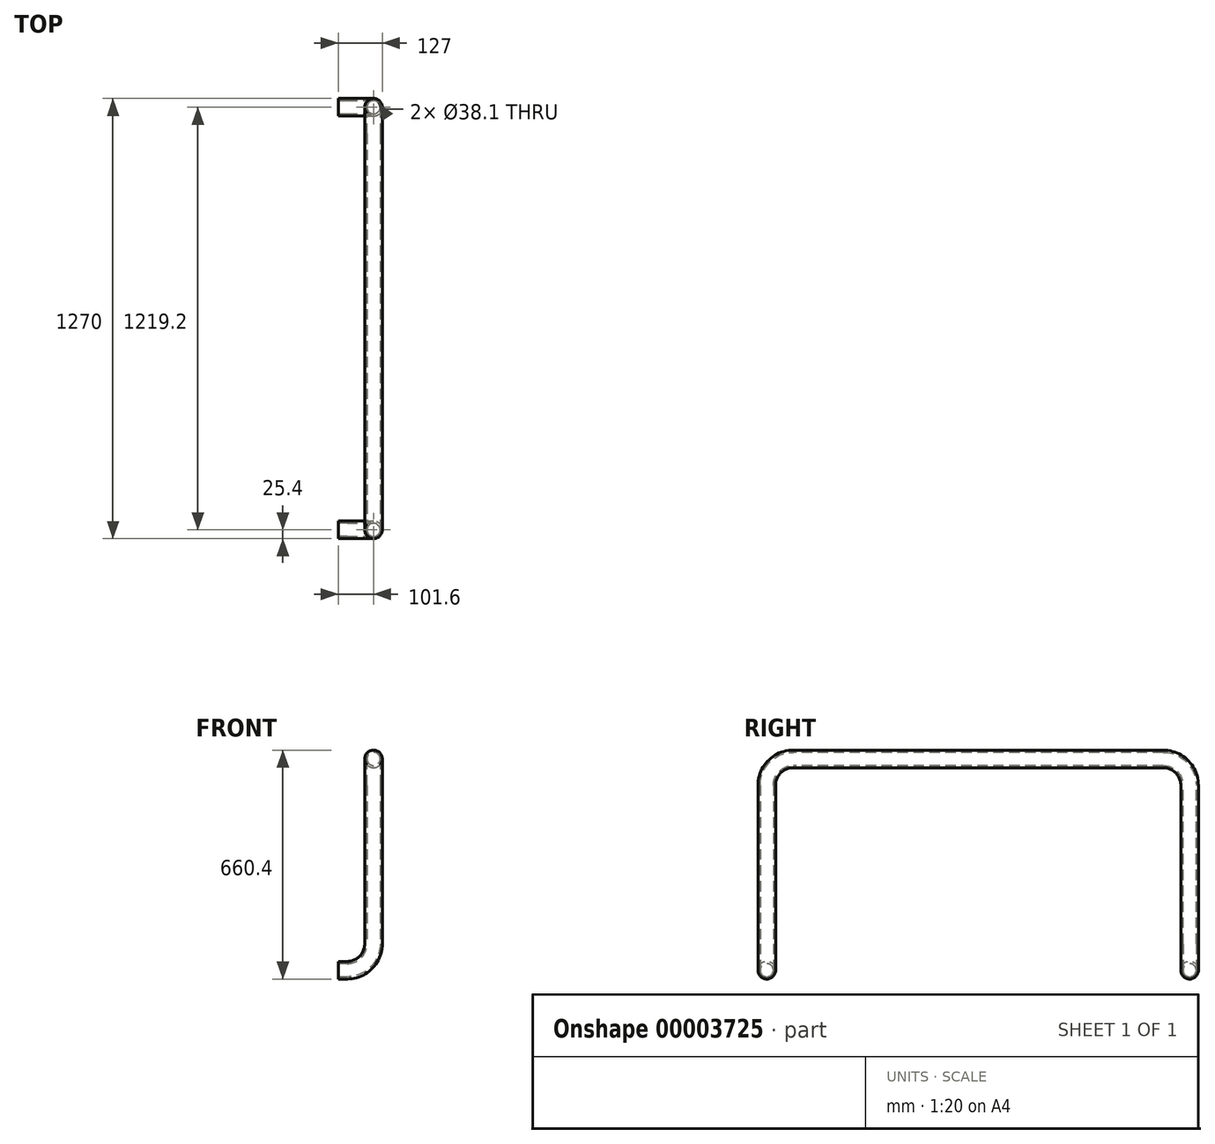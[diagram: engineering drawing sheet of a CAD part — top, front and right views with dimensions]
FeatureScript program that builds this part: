
annotation { "Feature Type Name" : "Feature", "Feature Type Description" : "" }
export const myFeature = defineFeature(function(context is Context, id is Id, definition is map)
    precondition{}
    {
        {
            var Q0;
            Q0=qCreatedBy(makeId("Right.planeOp"),FACE);
            var sketch = newSketch(context, id + "F0", { "sketchPlane" : qUnion([Q0])});
            skLineSegment(sketch, "E0", {"start": v(0, 52.09) * mm, "end": v(0, -46.01) * mm, "construction": true});
            skLineSegment(sketch, "E1", {"start": v(-47.96, 0) * mm, "end": v(47.23, 0) * mm, "construction": true});
            skLineSegment(sketch, "E2.0", {"start": v(-533.4, 304.8) * mm, "end": v(0, 304.8) * mm});
            skLineSegment(sketch, "E3.0", {"start": v(-47.96, -228.6) * mm, "end": v(47.23, -228.6) * mm, "construction": true});
            skLineSegment(sketch, "E4.0", {"start": v(-609.6, 228.6) * mm, "end": v(-609.6, -228.6) * mm});
            skPoint(sketch, "E5.visualSharp", {"position": v(-609.6, 304.8) * mm});
            skArc(sketch, "E5.filletArc", {"start": v(-533.4, 304.8) * mm, "mid": v(-587.28, 282.48) * mm, "end": v(-609.6, 228.6) * mm});
            skLineSegment(sketch, "E6.0.MirrorCS", {"start": v(533.4, 304.8) * mm, "end": v(0, 304.8) * mm});
            skArc(sketch, "E7.0.MirrorCS", {"start": v(533.4, 304.8) * mm, "mid": v(587.28, 282.48) * mm, "end": v(609.6, 228.6) * mm});
            skLineSegment(sketch, "E8.0.MirrorCS", {"start": v(609.6, 228.6) * mm, "end": v(609.6, -228.6) * mm});
            skSolve(sketch);
        }
        {
            var Q0;
            Q0=qCreatedBy(makeId("Front.planeOp"),FACE);
            cPlane(context, id + "F1", {"entities" : qUnion([Q0]), "cplaneType" : CPlaneType.OFFSET, "offset" : 609.6 * mm, "width" : 152.4 * mm, "height" : 152.4 * mm});
        }
        {
            var Q0;
            Q0=qCreatedBy(id+"F1.planeOp",FACE);
            var sketch = newSketch(context, id + "F2", { "sketchPlane" : qUnion([Q0])});
            skLineSegment(sketch, "E9.0", {"start": v(0, 228.6) * mm, "end": v(0, -228.6) * mm});
            skLineSegment(sketch, "E10", {"start": v(0, -228.6) * mm, "end": v(0, -228.6) * mm});
            skLineSegment(sketch, "E11", {"start": v(-76.2, -304.8) * mm, "end": v(-101.6, -304.8) * mm});
            skPoint(sketch, "E12.visualSharp", {"position": v(0, -304.8) * mm});
            skArc(sketch, "E12.filletArc", {"start": v(-76.2, -304.8) * mm, "mid": v(-22.32, -282.48) * mm, "end": v(0, -228.6) * mm});
            skSolve(sketch);
        }
        {
            var Q0;
            Q0=qCreatedBy(id+"F1.planeOp",FACE);
            cPlane(context, id + "F3", {"entities" : qUnion([Q0]), "cplaneType" : CPlaneType.OFFSET, "offset" : 1219.2 * mm, "oppositeDirection" : true, "width" : 152.4 * mm, "height" : 152.4 * mm});
        }
        {
            var Q0;
            Q0=qCreatedBy(id+"F3.planeOp",FACE);
            var sketch = newSketch(context, id + "F4", { "sketchPlane" : qUnion([Q0])});
            skLineSegment(sketch, "E13.0", {"start": v(0, 228.6) * mm, "end": v(0, -228.6) * mm});
            skArc(sketch, "E14.0", {"start": v(-76.2, -304.8) * mm, "mid": v(-22.32, -282.48) * mm, "end": v(0, -228.6) * mm});
            skLineSegment(sketch, "E15.0", {"start": v(-76.2, -304.8) * mm, "end": v(-101.6, -304.8) * mm});
            skSolve(sketch);
        }
        {
            var Q0;
            Q0=qCreatedBy(makeId("Right.planeOp"),FACE);
            cPlane(context, id + "F5", {"entities" : qUnion([Q0]), "cplaneType" : CPlaneType.OFFSET, "offset" : 101.6 * mm, "oppositeDirection" : true, "width" : 152.4 * mm, "height" : 152.4 * mm});
        }
        {
            var Q0;
            Q0=qCreatedBy(id+"F5.planeOp",FACE);
            var sketch = newSketch(context, id + "F6", { "sketchPlane" : qUnion([Q0])});
            skPoint(sketch, "E16.0", {"position": v(609.6, -304.8) * mm});
            skCircle(sketch, "E17", {"center": v(609.6, -304.8) * mm, "radius": 25.4 * mm});
            skCircle(sketch, "E18", {"center": v(609.6, -304.8) * mm, "radius": 19.05 * mm});
            skSolve(sketch);
        }
        {
            var Q0;
            Q0=makeQuery(id+"F6.imprint","IMPRINT",FACE,{"disambiguationData":[TD([[makeQuery(id+"F6.imprint","IMPRINT",EDGE,{"derivedFrom":sQuery(id+"F6.wireOp",EDGE,"E17")}),1.0]])]});
            var Q1;
            Q1=sQuery(id+"F4.wireOp",EDGE,"E15.0");
            var Q2;
            Q2=sQuery(id+"F4.wireOp",EDGE,"E14.0");
            var Q3;
            Q3=sQuery(id+"F4.wireOp",EDGE,"E13.0");
            var Q4;
            Q4=sQuery(id+"F0.wireOp",EDGE,"E7.0.MirrorCS");
            var Q5;
            Q5=sQuery(id+"F0.wireOp",EDGE,"E6.0.MirrorCS");
            var Q6;
            Q6=sQuery(id+"F0.wireOp",EDGE,"E2.0");
            var Q7;
            Q7=sQuery(id+"F0.wireOp",EDGE,"E5.filletArc");
            var Q8;
            Q8=sQuery(id+"F2.wireOp",EDGE,"E9.0");
            var Q9;
            Q9=sQuery(id+"F2.wireOp",EDGE,"E12.filletArc");
            var Q10;
            Q10=sQuery(id+"F2.wireOp",EDGE,"E11");
            sweep(context, id + "F7", {"profiles" : qUnion([Q0]), "path" : qUnion([Q1, Q2, Q3, Q4, Q5, Q6, Q7, Q8, Q9, Q10])});
        }
    });
